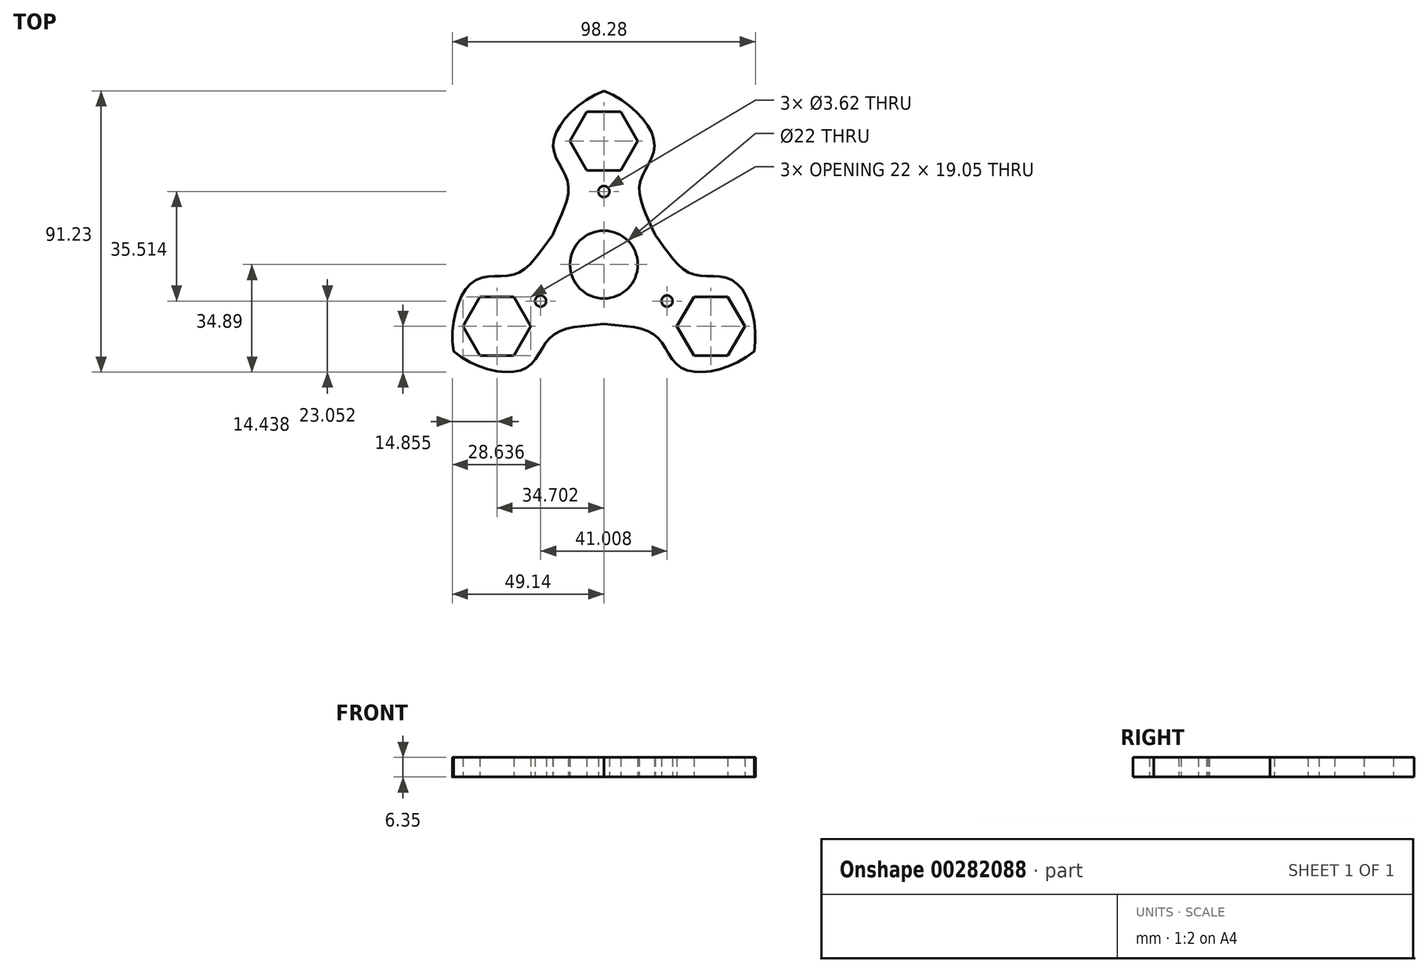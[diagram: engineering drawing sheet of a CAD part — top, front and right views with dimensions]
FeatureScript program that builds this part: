
annotation { "Feature Type Name" : "Feature", "Feature Type Description" : "" }
export const myFeature = defineFeature(function(context is Context, id is Id, definition is map)
    precondition{}
    {
        {
            var Q0;
            Q0=qCreatedBy(makeId("Top.planeOp"),FACE);
            var sketch = newSketch(context, id + "F0", { "sketchPlane" : qUnion([Q0])});
            skCircle(sketch, "E0", {"center": v(0, 0) * mm, "radius": 11 * mm});
            skCircle(sketch, "E1", {"center": v(0, 0) * mm, "radius": 19.2 * mm});
            skLineSegment(sketch, "E2", {"start": v(0, 0) * mm, "end": v(0, 80.14) * mm, "construction": true});
            skFitSpline(sketch, "E3", {"points": [v(0, 56.34) * mm, v(-16.44, 38.67) * mm, v(-11.58, 25.97) * mm, v(-16.74, 9.38) * mm], "startDerivative": vector(-69.44, -27.06) * mm, "endDerivative": vector(-20.24, -49.22) * mm});
            skFitSpline(sketch, "E4.MirrorCS", {"points": [v(0, 56.34) * mm, v(16.44, 38.67) * mm, v(11.58, 25.97) * mm, v(16.74, 9.38) * mm], "startDerivative": vector(69.44, -27.06) * mm, "endDerivative": vector(20.24, -49.22) * mm});
            skCircle(sketch, "E5", {"center": v(0, 23.68) * mm, "radius": 1.8 * mm});
            skCircle(sketch, "E6.cCircle", {"center": v(0, 40.07) * mm, "radius": 9.52 * mm, "construction": true});
            skLineSegment(sketch, "E6.0", {"start": v(5.5, 30.55) * mm, "end": v(-5.5, 30.55) * mm});
            skLineSegment(sketch, "E6.1", {"start": v(-5.5, 30.55) * mm, "end": v(-11, 40.07) * mm});
            skLineSegment(sketch, "E6.2", {"start": v(-11, 40.07) * mm, "end": v(-5.5, 49.6) * mm});
            skLineSegment(sketch, "E6.3", {"start": v(-5.5, 49.6) * mm, "end": v(5.5, 49.6) * mm});
            skLineSegment(sketch, "E6.4", {"start": v(5.5, 49.6) * mm, "end": v(11, 40.07) * mm});
            skLineSegment(sketch, "E6.5", {"start": v(11, 40.07) * mm, "end": v(5.5, 30.55) * mm});
            skPoint(sketch, "E6.0.midPoint", {"position": v(0, 30.55) * mm});
            skSolve(sketch);
        }
        {
            var Q0;
            Q0=makeQuery(id+"F0.imprint","IMPRINT",FACE,{"disambiguationData":[TD([[makeQuery(id+"F0.imprint","IMPRINT",EDGE,{"derivedFrom":sQuery(id+"F0.wireOp",EDGE,"E0")}),-1.0]])]});
            var Q1;
            Q1=makeQuery(id+"F0.imprint","IMPRINT",FACE,{"disambiguationData":[TD([[makeQuery(id+"F0.imprint","IMPRINT",EDGE,{"derivedFrom":sQuery(id+"F0.wireOp",EDGE,"EOAkcg2w-EWiD-yRF6-Ti1c-xLpTs7ueF0ee")}),-1.0]])]});
            var Q2;
            {var subQ1=sQuery(id+"F0.wireOp",EDGE,"E3");Q2=makeQuery(id+"F0.imprint","IMPRINT",FACE,{"disambiguationData":[TD([[makeQuery(id+"F0.imprint","IMPRINT",EDGE,{"derivedFrom":subQ1}),1.0]])]});}
            extrude(context, id + "F1", {"entities" : qUnion([Q0, Q1, Q2]), "depth" : 6.35 * mm});
        }
        {
            var Q0;
            Q0=makeQuery(id+"F1.opExtrude","SWEPT_BODY",BODY,{"disambiguationData":[OSD([sQuery(id+"F0.wireOp",EDGE,"E0"),sQuery(id+"F0.wireOp",EDGE,"EOAkcg2w-EWiD-yRF6-Ti1c-xLpTs7ueF0ee"),sQuery(id+"F0.wireOp",EDGE,"E1"),sQuery(id+"F0.wireOp",EDGE,"E3"),sQuery(id+"F0.wireOp",EDGE,"E4.MirrorCS")])]});
            var Q1;
            Q1=makeQuery(id+"F1.opExtrude","SWEPT_FACE",FACE,{"disambiguationData":[OSD([sQuery(id+"F0.wireOp",EDGE,"E0")])]});
            circularPattern(context, id + "F2", {"operationType" : NewBodyOperationType.ADD, "entities" : qUnion([Q0]), "axis" : qUnion([Q1]), "angle" : 360 * degree, "instanceCount" : 3, "equalSpace" : true});
        }
    });
